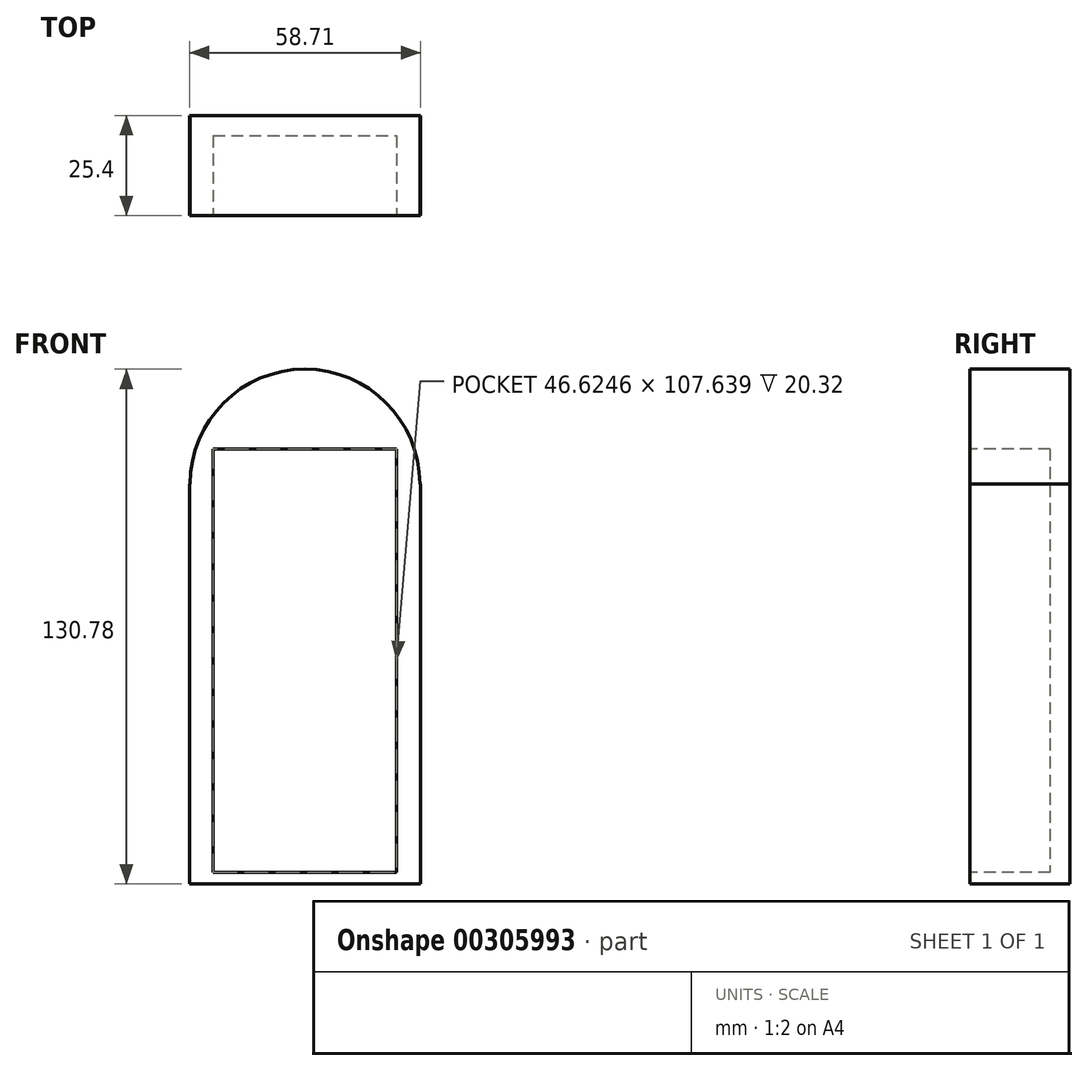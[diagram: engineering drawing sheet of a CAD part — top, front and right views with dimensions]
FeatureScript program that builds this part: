
annotation { "Feature Type Name" : "Feature", "Feature Type Description" : "" }
export const myFeature = defineFeature(function(context is Context, id is Id, definition is map)
    precondition{}
    {
        {
            var Q0;
            Q0=qCreatedBy(makeId("Front.planeOp"),FACE);
            var sketch = newSketch(context, id + "F0", { "sketchPlane" : qUnion([Q0])});
            skLineSegment(sketch, "E0.bottom", {"start": v(-58.71, 25.61) * mm, "end": v(-58.54, 25.61) * mm});
            skLineSegment(sketch, "E0.top", {"start": v(-58.71, -75.98) * mm, "end": v(0, -75.98) * mm});
            skLineSegment(sketch, "E0.left", {"start": v(-58.71, 25.61) * mm, "end": v(-58.71, -75.98) * mm});
            skLineSegment(sketch, "E0.right", {"start": v(0, 25.61) * mm, "end": v(0, -75.98) * mm});
            skArc(sketch, "E1", {"start": v(-0.18, 25.61) * mm, "mid": v(-29.36, 54.8) * mm, "end": v(-58.54, 25.61) * mm});
            skLineSegment(sketch, "E2.trimOffspring", {"start": v(-0.18, 25.61) * mm, "end": v(0, 25.61) * mm});
            skSolve(sketch);
        }
        {
            var Q0;
            Q0 = qSketchRegion(id + "F0", true);
            extrude(context, id + "F1", {"entities" : qUnion([Q0]), "depth" : 25.4 * mm});
        }
        {
            var Q0;
            Q0=makeQuery(id+"F1.opExtrude","CAP_FACE",FACE,{"disambiguationData":[OSD([sQuery(id+"F0.wireOp",EDGE,"E0.bottom"),sQuery(id+"F0.wireOp",EDGE,"E0.top"),sQuery(id+"F0.wireOp",EDGE,"E0.left"),sQuery(id+"F0.wireOp",EDGE,"E0.right"),sQuery(id+"F0.wireOp",EDGE,"E1"),sQuery(id+"F0.wireOp",EDGE,"E2.trimOffspring")])],"isStart":false});
            var sketch = newSketch(context, id + "F2", { "sketchPlane" : qUnion([Q0])});
            skLineSegment(sketch, "E3.bottom", {"start": v(-52.67, 34.54) * mm, "end": v(-6.04, 34.54) * mm});
            skLineSegment(sketch, "E3.top", {"start": v(-52.67, -73.1) * mm, "end": v(-6.04, -73.1) * mm});
            skLineSegment(sketch, "E3.left", {"start": v(-52.67, 34.54) * mm, "end": v(-52.67, -73.1) * mm});
            skLineSegment(sketch, "E3.right", {"start": v(-6.04, 34.54) * mm, "end": v(-6.04, -73.1) * mm});
            skSolve(sketch);
        }
        {
            var Q0;
            Q0 = qSketchRegion(id + "F2", true);
            extrude(context, id + "F3", {"entities" : qUnion([Q0]), "operationType" : NewBodyOperationType.REMOVE, "oppositeDirection" : true, "depth" : 20.32 * mm});
        }
    });
